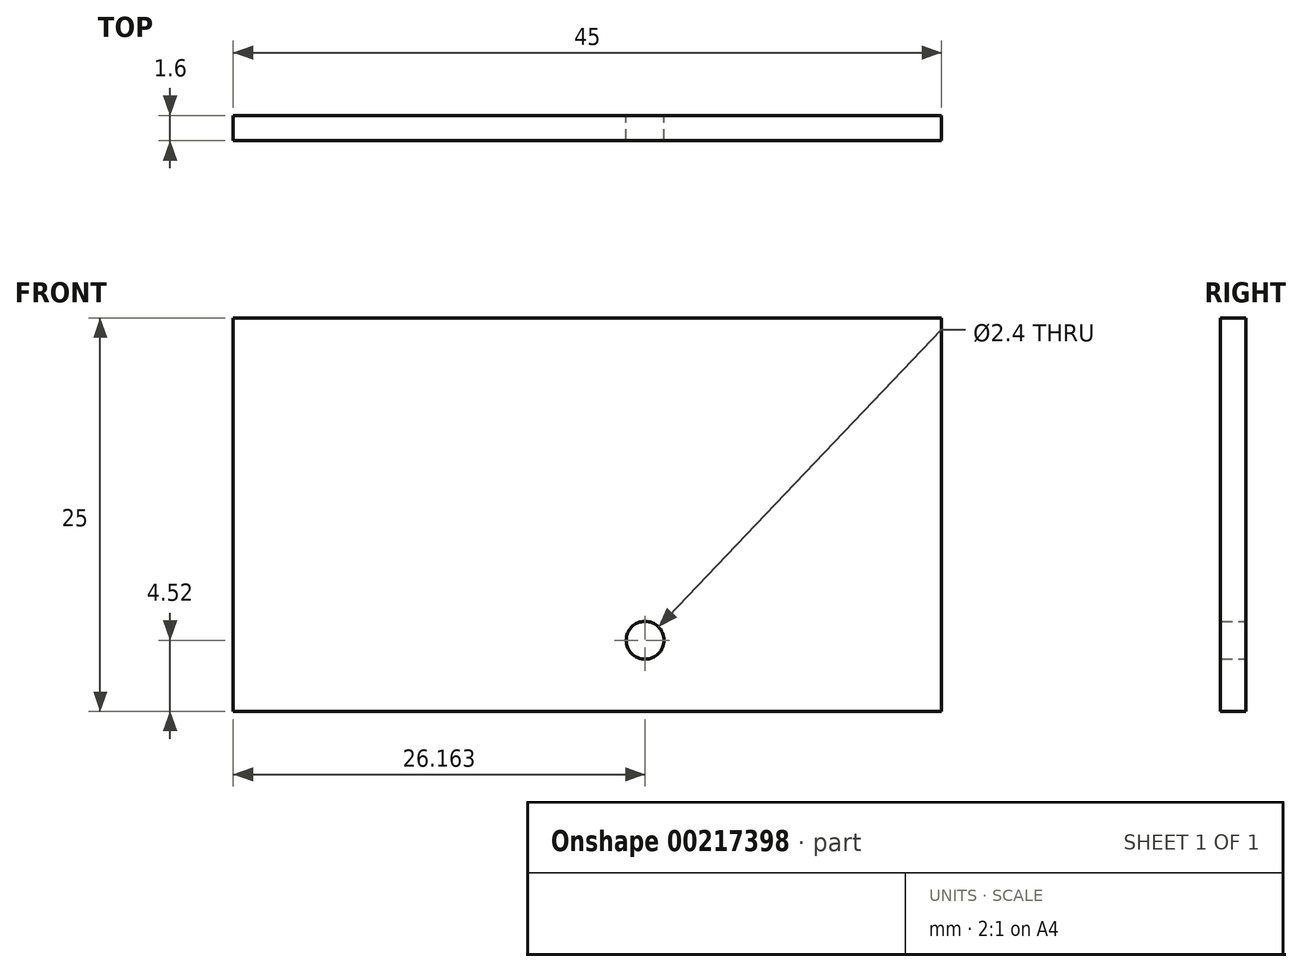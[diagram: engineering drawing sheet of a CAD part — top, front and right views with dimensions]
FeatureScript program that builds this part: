
annotation { "Feature Type Name" : "Feature", "Feature Type Description" : "" }
export const myFeature = defineFeature(function(context is Context, id is Id, definition is map)
    precondition{}
    {
        {
            var Q0;
            Q0=qCreatedBy(makeId("Front.planeOp"),FACE);
            var sketch = newSketch(context, id + "F0", { "sketchPlane" : qUnion([Q0])});
            skLineSegment(sketch, "E0.bottom", {"start": v(22.5, 12.5) * mm, "end": v(-22.5, 12.5) * mm});
            skLineSegment(sketch, "E0.top", {"start": v(22.5, -12.5) * mm, "end": v(-22.5, -12.5) * mm});
            skLineSegment(sketch, "E0.left", {"start": v(22.5, 12.5) * mm, "end": v(22.5, -12.5) * mm});
            skLineSegment(sketch, "E0.right", {"start": v(-22.5, 12.5) * mm, "end": v(-22.5, -12.5) * mm});
            skPoint(sketch, "E0.middle", {"position": v(0, 0) * mm});
            skSolve(sketch);
        }
        {
            var Q0;
            Q0 = qSketchRegion(id + "F0", true);
            extrude(context, id + "F1", {"entities" : qUnion([Q0]), "oppositeDirection" : true, "depth" : 1.6 * mm});
        }
        {
            var Q0;
            Q0=makeQuery(id+"F1.opExtrude","CAP_FACE",FACE,{"disambiguationData":[OSD([sQuery(id+"F0.wireOp",EDGE,"E0.bottom"),sQuery(id+"F0.wireOp",EDGE,"E0.top"),sQuery(id+"F0.wireOp",EDGE,"E0.left"),sQuery(id+"F0.wireOp",EDGE,"E0.right")])],"isStart":true});
            var sketch = newSketch(context, id + "F2", { "sketchPlane" : qUnion([Q0])});
            skText(sketch, "E1", { "text": "HV-702", "fontName": "OpenSans-Regular.ttf"});
            skLineSegment(sketch, "E2", {"start": v(0, 12.5) * mm, "end": v(0, -9.1) * mm, "construction": true});
            skPoint(sketch, "E2.endSnap0", {"position": v(0, 12.5) * mm});
            skLineSegment(sketch, "E3", {"start": v(-22.5, 6) * mm, "end": v(22.5, 6) * mm, "construction": true});
            skLineSegment(sketch, "E4", {"start": v(-22.5, 0) * mm, "end": v(22.5, 0) * mm, "construction": true});
            skLineSegment(sketch, "E5", {"start": v(-22.5, -5.5) * mm, "end": v(22.5, -5.5) * mm, "construction": true});
            skLineSegment(sketch, "E6", {"start": v(-22.5, -10.5) * mm, "end": v(22.5, -10.5) * mm, "construction": true});
            skText(sketch, "E7", { "text": "Test", "fontName": "OpenSans-Regular.ttf"});
            const initialGuessF2  = {"E1": [-0.01174, 0.006, 1, 0, 0.005], "E7": [-0.01855, 0, 1, 0, 0.00357]};
            skSetInitialGuess(sketch, initialGuessF2);
            skSolve(sketch);
        }
        {
            var Q0;
            Q0=makeQuery(id+"F2.imprint","IMPRINT",FACE,{"disambiguationData":[TD([[makeQuery(id+"F2.imprint","IMPRINT",EDGE,{"derivedFrom":sQuery(id+"F2.wireOp",EDGE,"E1.sketch_text.stroke-0")}),1.0]])]});
            var sketch = newSketch(context, id + "F3", { "sketchPlane" : qUnion([Q0])});
            skPoint(sketch, "E8", {"position": v(3.66, -7.98) * mm});
            skSolve(sketch);
        }
        {
            var Q0;
            Q0=sQuery(id+"F3.wireOp",VERTEX,"E8");
            var Q1;
            Q1=makeQuery(id+"F1.opExtrude","SWEPT_BODY",BODY,{"disambiguationData":[OSD([sQuery(id+"F0.wireOp",EDGE,"E0.bottom"),sQuery(id+"F0.wireOp",EDGE,"E0.top"),sQuery(id+"F0.wireOp",EDGE,"E0.left"),sQuery(id+"F0.wireOp",EDGE,"E0.right")])]});
            hole(context, id + "F4", {"style" : HoleStyle.SIMPLE, "endStyle" : HoleEndStyle.THROUGH, "standardTappedOrClearance" : lookupTablePath({ "standard" : "ISO", "engagement" : "75%", "pitch" : "0.6 mm", "size" : "M3", "type" : "Tapped" }), "standardBlindInLast" : lookupTablePath({ "standard" : "ISO", "engagement" : "75%", "pitch" : "0.6 mm", "size" : "M3", "type" : "Tapped" }), "holeDiameter" : 2.4 * mm, "showTappedDepth" : true, "tappedDepth" : 6 * mm, "tapClearance" : 2, "locations" : qUnion([Q0]), "scope" : qUnion([Q1])});
        }
    });
